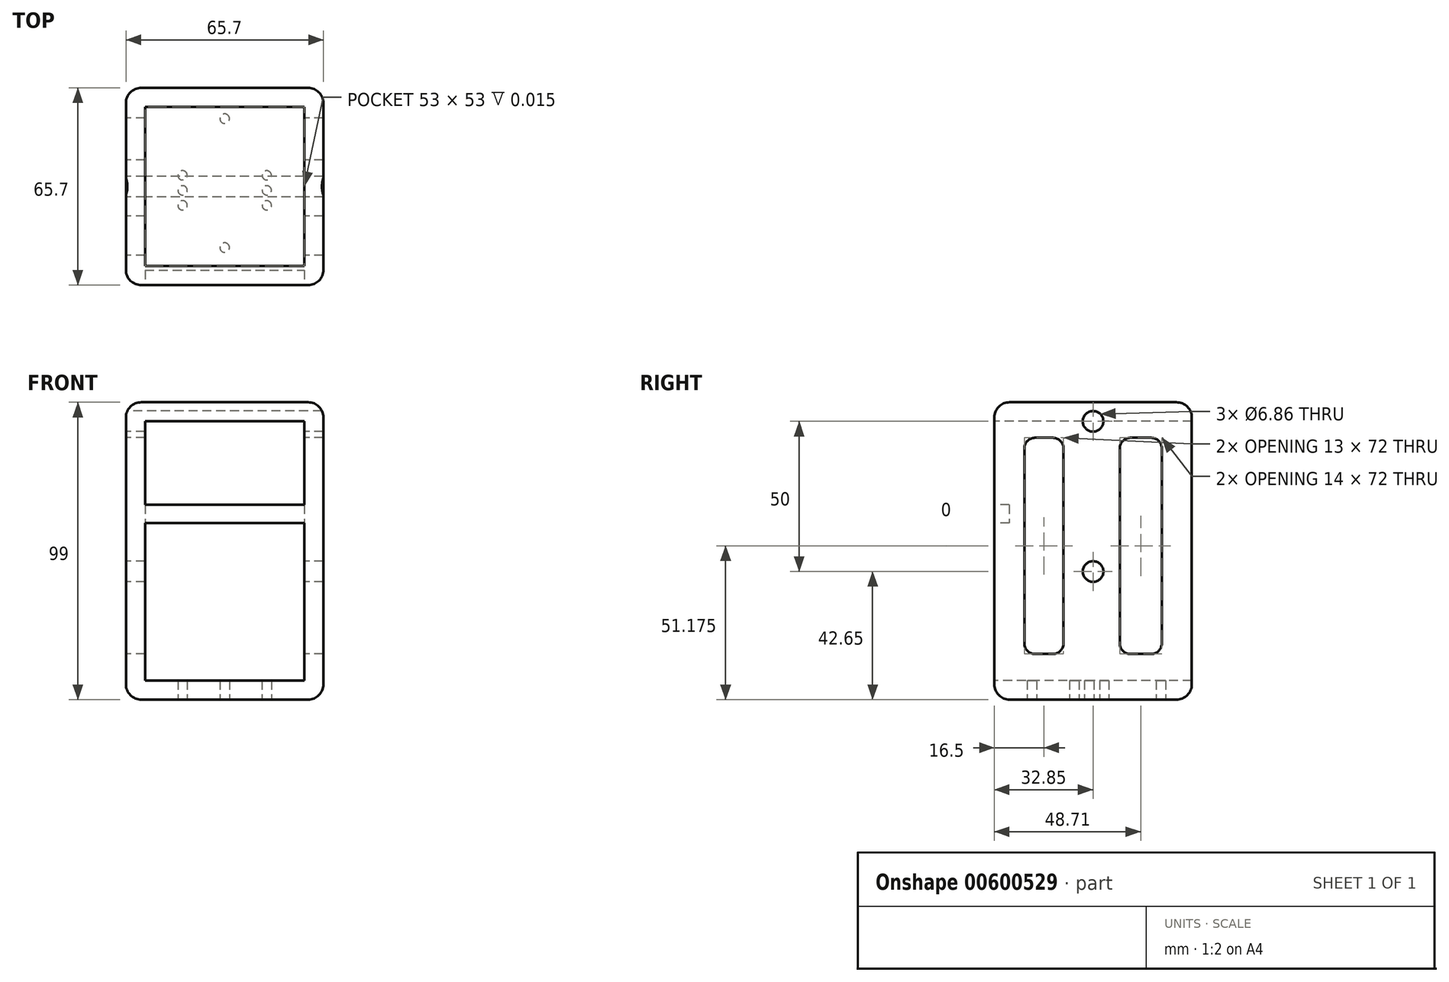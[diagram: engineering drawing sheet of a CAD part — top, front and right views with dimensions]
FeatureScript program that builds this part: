
annotation { "Feature Type Name" : "Feature", "Feature Type Description" : "" }
export const myFeature = defineFeature(function(context is Context, id is Id, definition is map)
    precondition{}
    {
        {
            var Q0;
            Q0=qCreatedBy(makeId("Top.planeOp"),FACE);
            var sketch = newSketch(context, id + "F0", { "sketchPlane" : qUnion([Q0])});
            skLineSegment(sketch, "E0.bottom", {"start": v(32.85, -32.85) * mm, "end": v(-32.85, -32.85) * mm});
            skLineSegment(sketch, "E0.top", {"start": v(32.85, 32.85) * mm, "end": v(-32.85, 32.85) * mm});
            skLineSegment(sketch, "E0.left", {"start": v(32.85, -32.85) * mm, "end": v(32.85, 32.85) * mm});
            skLineSegment(sketch, "E0.right", {"start": v(-32.85, -32.85) * mm, "end": v(-32.85, 32.85) * mm});
            skPoint(sketch, "E0.middle", {"position": v(0, 0) * mm});
            skLineSegment(sketch, "E1.bottom", {"start": v(26.5, -26.5) * mm, "end": v(-26.5, -26.5) * mm});
            skLineSegment(sketch, "E1.top", {"start": v(26.5, 26.5) * mm, "end": v(-26.5, 26.5) * mm});
            skLineSegment(sketch, "E1.left", {"start": v(26.5, -26.5) * mm, "end": v(26.5, 26.5) * mm});
            skLineSegment(sketch, "E1.right", {"start": v(-26.5, -26.5) * mm, "end": v(-26.5, 26.5) * mm});
            skLineSegment(sketch, "E2", {"start": v(-26.5, -24) * mm, "end": v(-26.5, -26.5) * mm});
            skSolve(sketch);
        }
        {
            var Q0;
            Q0 = qSketchRegion(id + "F0", true);
            extrude(context, id + "F1", {"entities" : qUnion([Q0]), "depth" : 1 / 203.2 * mm, "offsetDistance" : 25.4 * mm});
        }
        {
            var Q0;
            Q0=makeQuery(id+"F1.opExtrude","SWEPT_FACE",FACE,{"disambiguationData":[OSD([sQuery(id+"F0.wireOp",EDGE,"E0.bottom")])]});
            var sketch = newSketch(context, id + "F2", { "sketchPlane" : qUnion([Q0])});
            skLineSegment(sketch, "E3.bottom", {"start": v(-32.85, 0) * mm, "end": v(32.85, 0) * mm});
            skLineSegment(sketch, "E3.top", {"start": v(-32.85, -99) * mm, "end": v(32.85, -99) * mm});
            skLineSegment(sketch, "E3.left", {"start": v(-32.85, 0) * mm, "end": v(-32.85, -99) * mm});
            skLineSegment(sketch, "E3.right", {"start": v(32.85, 0) * mm, "end": v(32.85, -99) * mm});
            skLineSegment(sketch, "E4.bottom", {"start": v(-26.5, -6.35) * mm, "end": v(26.5, -6.35) * mm});
            skLineSegment(sketch, "E4.top", {"start": v(-26.5, -92.65) * mm, "end": v(26.5, -92.65) * mm});
            skLineSegment(sketch, "E4.left", {"start": v(-26.5, -6.35) * mm, "end": v(-26.5, -92.65) * mm});
            skLineSegment(sketch, "E4.right", {"start": v(26.5, -6.35) * mm, "end": v(26.5, -92.65) * mm});
            skSolve(sketch);
        }
        {
            var Q0;
            Q0=makeQuery(id+"F2.imprint","IMPRINT",FACE,{"disambiguationData":[TD([[makeQuery(id+"F2.imprint","IMPRINT",EDGE,{"derivedFrom":sQuery(id+"F2.wireOp",EDGE,"E3.bottom")}),1.0]])]});
            extrude(context, id + "F3", {"entities" : qUnion([Q0]), "operationType" : NewBodyOperationType.ADD, "oppositeDirection" : true, "depth" : 65.7 * mm, "offsetDistance" : 25.4 * mm});
        }
        {
            var Q0;
            Q0=makeQuery(id+"F3.boolean.opBoolean","SPLIT",FACE,{"disambiguationData":[TD([makeQuery(id+"F1.opExtrude","SWEPT_FACE",FACE,{"disambiguationData":[OSD([sQuery(id+"F0.wireOp",EDGE,"E1.bottom")])]})])],"derivedFrom":makeQuery(id+"F3.opExtrude","SWEPT_FACE",FACE,{"disambiguationData":[OSD([sQuery(id+"F2.wireOp",EDGE,"E3.bottom")])]})});
            var Q1;
            Q1=makeQuery(id+"F3.boolean.opBoolean","SPLIT",FACE,{"disambiguationData":[TD([makeQuery(id+"F1.opExtrude","SWEPT_FACE",FACE,{"disambiguationData":[OSD([sQuery(id+"F0.wireOp",EDGE,"E1.top")])]})])],"derivedFrom":makeQuery(id+"F3.opExtrude","SWEPT_FACE",FACE,{"disambiguationData":[OSD([sQuery(id+"F2.wireOp",EDGE,"E3.bottom")])]})});
            extrude(context, id + "F4", {"entities" : qUnion([Q0, Q1]), "operationType" : NewBodyOperationType.REMOVE, "oppositeDirection" : true, "depth" : 1 / 101.6 * mm, "offsetDistance" : 25.4 * mm});
        }
        {
            var Q0;
            Q0=makeQuery(id+"F3.boolean.opBoolean","MERGE",FACE,{"derivedFrom":[makeQuery(id+"F1.opExtrude","SWEPT_FACE",FACE,{"disambiguationData":[OSD([sQuery(id+"F0.wireOp",EDGE,"E0.right")])]}),makeQuery(id+"F3.opExtrude","SWEPT_FACE",FACE,{"disambiguationData":[OSD([sQuery(id+"F2.wireOp",EDGE,"E3.left")])]})]});
            var sketch = newSketch(context, id + "F5", { "sketchPlane" : qUnion([Q0])});
            skCircle(sketch, "E5", {"center": v(0, -56.35) * mm, "radius": 3.43 * mm});
            skCircle(sketch, "E6", {"center": v(0, -6.35) * mm, "radius": 3.43 * mm});
            skLineSegment(sketch, "E7.bottom", {"start": v(19.35, -11.82) * mm, "end": v(13.35, -11.83) * mm});
            skLineSegment(sketch, "E7.top", {"start": v(19.35, -83.83) * mm, "end": v(13.35, -83.83) * mm});
            skLineSegment(sketch, "E7.left", {"start": v(22.85, -15.32) * mm, "end": v(22.85, -80.33) * mm});
            skLineSegment(sketch, "E7.right", {"start": v(9.85, -15.32) * mm, "end": v(9.85, -80.33) * mm});
            skLineSegment(sketch, "E8.bottom", {"start": v(-12.36, -11.82) * mm, "end": v(-19.36, -11.82) * mm});
            skLineSegment(sketch, "E8.top", {"start": v(-12.36, -83.83) * mm, "end": v(-19.36, -83.83) * mm});
            skLineSegment(sketch, "E8.left", {"start": v(-8.86, -15.32) * mm, "end": v(-8.86, -80.33) * mm});
            skLineSegment(sketch, "E8.right", {"start": v(-22.86, -15.32) * mm, "end": v(-22.86, -80.33) * mm});
            skPoint(sketch, "E9.visualSharp", {"position": v(22.85, -11.82) * mm});
            skArc(sketch, "E9.filletArc", {"start": v(22.85, -15.32) * mm, "mid": v(21.82, -12.85) * mm, "end": v(19.35, -11.83) * mm});
            skPoint(sketch, "E10.visualSharp", {"position": v(9.85, -11.82) * mm});
            skArc(sketch, "E10.filletArc", {"start": v(13.35, -11.83) * mm, "mid": v(10.88, -12.85) * mm, "end": v(9.85, -15.33) * mm});
            skPoint(sketch, "E11.visualSharp", {"position": v(22.85, -83.83) * mm});
            skArc(sketch, "E11.filletArc", {"start": v(19.35, -83.83) * mm, "mid": v(21.82, -82.8) * mm, "end": v(22.85, -80.33) * mm});
            skPoint(sketch, "E12.visualSharp", {"position": v(9.85, -83.83) * mm});
            skArc(sketch, "E12.filletArc", {"start": v(9.85, -80.33) * mm, "mid": v(10.88, -82.8) * mm, "end": v(13.35, -83.83) * mm});
            skPoint(sketch, "E13.visualSharp", {"position": v(-8.86, -83.83) * mm});
            skArc(sketch, "E13.filletArc", {"start": v(-12.36, -83.83) * mm, "mid": v(-9.89, -82.8) * mm, "end": v(-8.86, -80.33) * mm});
            skPoint(sketch, "E14.visualSharp", {"position": v(-22.86, -83.83) * mm});
            skArc(sketch, "E14.filletArc", {"start": v(-22.86, -80.33) * mm, "mid": v(-21.83, -82.8) * mm, "end": v(-19.36, -83.83) * mm});
            skPoint(sketch, "E15.visualSharp", {"position": v(-22.86, -11.82) * mm});
            skArc(sketch, "E15.filletArc", {"start": v(-19.36, -11.82) * mm, "mid": v(-21.83, -12.85) * mm, "end": v(-22.86, -15.32) * mm});
            skPoint(sketch, "E16.visualSharp", {"position": v(-8.86, -11.82) * mm});
            skArc(sketch, "E16.filletArc", {"start": v(-8.86, -15.32) * mm, "mid": v(-9.89, -12.85) * mm, "end": v(-12.36, -11.82) * mm});
            skSolve(sketch);
        }
        {
            var Q0;
            Q0 = qSketchRegion(id + "F5", true);
            extrude(context, id + "F6", {"entities" : qUnion([Q0]), "operationType" : NewBodyOperationType.REMOVE, "endBound" : BoundingType.THROUGH_ALL, "oppositeDirection" : true, "depth" : 25.4 * mm, "offsetDistance" : 25.4 * mm});
        }
        {
            var Q0;
            Q0=makeQuery(id+"F1.opExtrude","CAP_EDGE",EDGE,{"disambiguationData":[OSD([sQuery(id+"F0.wireOp",EDGE,"E0.bottom")])],"isStart":false});
            var Q1;
            Q1=makeQuery(id+"F1.opExtrude","CAP_EDGE",EDGE,{"disambiguationData":[OSD([sQuery(id+"F0.wireOp",EDGE,"E0.left")])],"isStart":false});
            var Q2;
            Q2=makeQuery(id+"F1.opExtrude","CAP_EDGE",EDGE,{"disambiguationData":[OSD([sQuery(id+"F0.wireOp",EDGE,"E0.top")])],"isStart":false});
            var Q3;
            Q3=makeQuery(id+"F1.opExtrude","CAP_EDGE",EDGE,{"disambiguationData":[OSD([sQuery(id+"F0.wireOp",EDGE,"E0.right")])],"isStart":false});
            var Q4;
            Q4=makeQuery(id+"F3.boolean.opBoolean","MERGE",EDGE,{"derivedFrom":[makeQuery(id+"F1.opExtrude","SWEPT_EDGE",EDGE,{"disambiguationData":[OSD([sQuery(id+"F0.wireOp",EDGE,"E0.top"),sQuery(id+"F0.wireOp",EDGE,"E0.left")])]}),makeQuery(id+"F3.opExtrude","CAP_EDGE",EDGE,{"disambiguationData":[OSD([sQuery(id+"F2.wireOp",EDGE,"E3.right")])],"isStart":false})]});
            var Q5;
            Q5=makeQuery(id+"F3.boolean.opBoolean","MERGE",EDGE,{"derivedFrom":[makeQuery(id+"F1.opExtrude","SWEPT_EDGE",EDGE,{"disambiguationData":[OSD([sQuery(id+"F0.wireOp",EDGE,"E0.bottom"),sQuery(id+"F0.wireOp",EDGE,"E0.left")])]}),makeQuery(id+"F3.opExtrude","CAP_EDGE",EDGE,{"disambiguationData":[OSD([sQuery(id+"F2.wireOp",EDGE,"E3.right")])],"isStart":true})]});
            var Q6;
            Q6=makeQuery(id+"F3.boolean.opBoolean","MERGE",EDGE,{"derivedFrom":[makeQuery(id+"F1.opExtrude","SWEPT_EDGE",EDGE,{"disambiguationData":[OSD([sQuery(id+"F0.wireOp",EDGE,"E0.bottom"),sQuery(id+"F0.wireOp",EDGE,"E0.right")])]}),makeQuery(id+"F3.opExtrude","CAP_EDGE",EDGE,{"disambiguationData":[OSD([sQuery(id+"F2.wireOp",EDGE,"E3.left")])],"isStart":true})]});
            var Q7;
            Q7=makeQuery(id+"F3.boolean.opBoolean","MERGE",EDGE,{"derivedFrom":[makeQuery(id+"F1.opExtrude","SWEPT_EDGE",EDGE,{"disambiguationData":[OSD([sQuery(id+"F0.wireOp",EDGE,"E0.top"),sQuery(id+"F0.wireOp",EDGE,"E0.right")])]}),makeQuery(id+"F3.opExtrude","CAP_EDGE",EDGE,{"disambiguationData":[OSD([sQuery(id+"F2.wireOp",EDGE,"E3.left")])],"isStart":false})]});
            var Q8;
            Q8=makeQuery(id+"F3.opExtrude","CAP_EDGE",EDGE,{"disambiguationData":[OSD([sQuery(id+"F2.wireOp",EDGE,"E3.top")])],"isStart":false});
            var Q9;
            Q9=makeQuery(id+"F3.opExtrude","SWEPT_EDGE",EDGE,{"disambiguationData":[OSD([sQuery(id+"F2.wireOp",EDGE,"E3.top"),sQuery(id+"F2.wireOp",EDGE,"E3.left")])]});
            var Q10;
            Q10=makeQuery(id+"F3.opExtrude","SWEPT_EDGE",EDGE,{"disambiguationData":[OSD([sQuery(id+"F2.wireOp",EDGE,"E3.top"),sQuery(id+"F2.wireOp",EDGE,"E3.right")])]});
            var Q11;
            Q11=makeQuery(id+"F3.opExtrude","CAP_EDGE",EDGE,{"disambiguationData":[OSD([sQuery(id+"F2.wireOp",EDGE,"E3.top")])],"isStart":true});
            fillet(context, id + "F7", {"entities" : qUnion([Q0, Q1, Q2, Q3, Q4, Q5, Q6, Q7, Q8, Q9, Q10, Q11]), "radius" : 5.08 * mm, "tangentPropagation" : true, "allowEdgeOverflow" : false});
        }
        {
            var Q0;
            Q0=makeQuery(id+"F3.boolean.opBoolean","MERGE",FACE,{"derivedFrom":[makeQuery(id+"F1.opExtrude","SWEPT_FACE",FACE,{"disambiguationData":[OSD([sQuery(id+"F0.wireOp",EDGE,"E0.bottom")])]}),makeQuery(id+"F3.opExtrude","CAP_FACE",FACE,{"disambiguationData":[OSD([sQuery(id+"F2.wireOp",EDGE,"E3.bottom"),sQuery(id+"F2.wireOp",EDGE,"E3.top"),sQuery(id+"F2.wireOp",EDGE,"E3.left"),sQuery(id+"F2.wireOp",EDGE,"E3.right"),sQuery(id+"F2.wireOp",EDGE,"E4.bottom"),sQuery(id+"F2.wireOp",EDGE,"E4.top"),sQuery(id+"F2.wireOp",EDGE,"E4.left"),sQuery(id+"F2.wireOp",EDGE,"E4.right")])],"isStart":true})]});
            var sketch = newSketch(context, id + "F8", { "sketchPlane" : qUnion([Q0])});
            skLineSegment(sketch, "E17", {"start": v(-26.5, -34.15) * mm, "end": v(26.5, -34.15) * mm});
            skLineSegment(sketch, "E18", {"start": v(26.5, -34.15) * mm, "end": v(26.5, -40.15) * mm});
            skLineSegment(sketch, "E19", {"start": v(-26.5, -40.15) * mm, "end": v(26.5, -40.15) * mm});
            skLineSegment(sketch, "E20", {"start": v(-26.5, -34.15) * mm, "end": v(-26.5, -40.15) * mm});
            skSolve(sketch);
        }
        {
            var Q0;
            Q0=makeQuery(id+"F8.imprint","IMPRINT",FACE,{"disambiguationData":[TD([[makeQuery(id+"F8.imprint","IMPRINT",EDGE,{"derivedFrom":sQuery(id+"F8.wireOp",EDGE,"E17")}),-1.0]])]});
            extrude(context, id + "F9", {"entities" : qUnion([Q0]), "operationType" : NewBodyOperationType.ADD, "oppositeDirection" : true, "depth" : 5 * mm, "offsetDistance" : 25 * mm});
        }
        {
            var Q0;
            Q0=makeQuery(id+"F3.opExtrude","SWEPT_FACE",FACE,{"disambiguationData":[OSD([sQuery(id+"F2.wireOp",EDGE,"E3.top")])]});
            var sketch = newSketch(context, id + "F10", { "sketchPlane" : qUnion([Q0])});
            skCircle(sketch, "E21", {"center": v(0, 20.32) * mm, "radius": 1.59 * mm});
            skLineSegment(sketch, "E22", {"start": v(-27.77, 27.77) * mm, "end": v(-14.02, 27.77) * mm});
            skLineSegment(sketch, "E23", {"start": v(14.02, 27.77) * mm, "end": v(27.77, 27.77) * mm});
            skLineSegment(sketch, "E24", {"start": v(0, 3.43) * mm, "end": v(0, 4.87) * mm});
            skCircle(sketch, "E25", {"center": v(-14.02, 1.28) * mm, "radius": 1.55 * mm});
            skCircle(sketch, "E26", {"center": v(14.02, 1.28) * mm, "radius": 1.55 * mm});
            skLineSegment(sketch, "E27", {"start": v(-14.02, 27.77) * mm, "end": v(14.02, 27.77) * mm});
            skCircle(sketch, "E28", {"center": v(-14.02, 6.28) * mm, "radius": 1.55 * mm});
            skCircle(sketch, "E29", {"center": v(-14.02, -3.72) * mm, "radius": 1.55 * mm});
            skCircle(sketch, "E30", {"center": v(14.02, 6.28) * mm, "radius": 1.55 * mm});
            skCircle(sketch, "E31", {"center": v(14.02, -3.72) * mm, "radius": 1.55 * mm});
            skLineSegment(sketch, "E32", {"start": v(27.77, 1.28) * mm, "end": v(27.77, 27.77) * mm});
            skLineSegment(sketch, "E33", {"start": v(27.77, 1.28) * mm, "end": v(27.77, -27.77) * mm});
            skLineSegment(sketch, "E34", {"start": v(-27.77, 27.77) * mm, "end": v(-27.77, 1.28) * mm});
            skLineSegment(sketch, "E35", {"start": v(-27.77, 1.28) * mm, "end": v(-27.77, -27.77) * mm});
            skCircle(sketch, "E36", {"center": v(0, -22.6) * mm, "radius": 1.59 * mm});
            skSolve(sketch);
        }
        {
            var Q0;
            Q0 = qSketchRegion(id + "F10", true);
            extrude(context, id + "F11", {"entities" : qUnion([Q0]), "operationType" : NewBodyOperationType.REMOVE, "oppositeDirection" : true, "depth" : 10 * mm, "offsetDistance" : 25 * mm});
        }
    });
